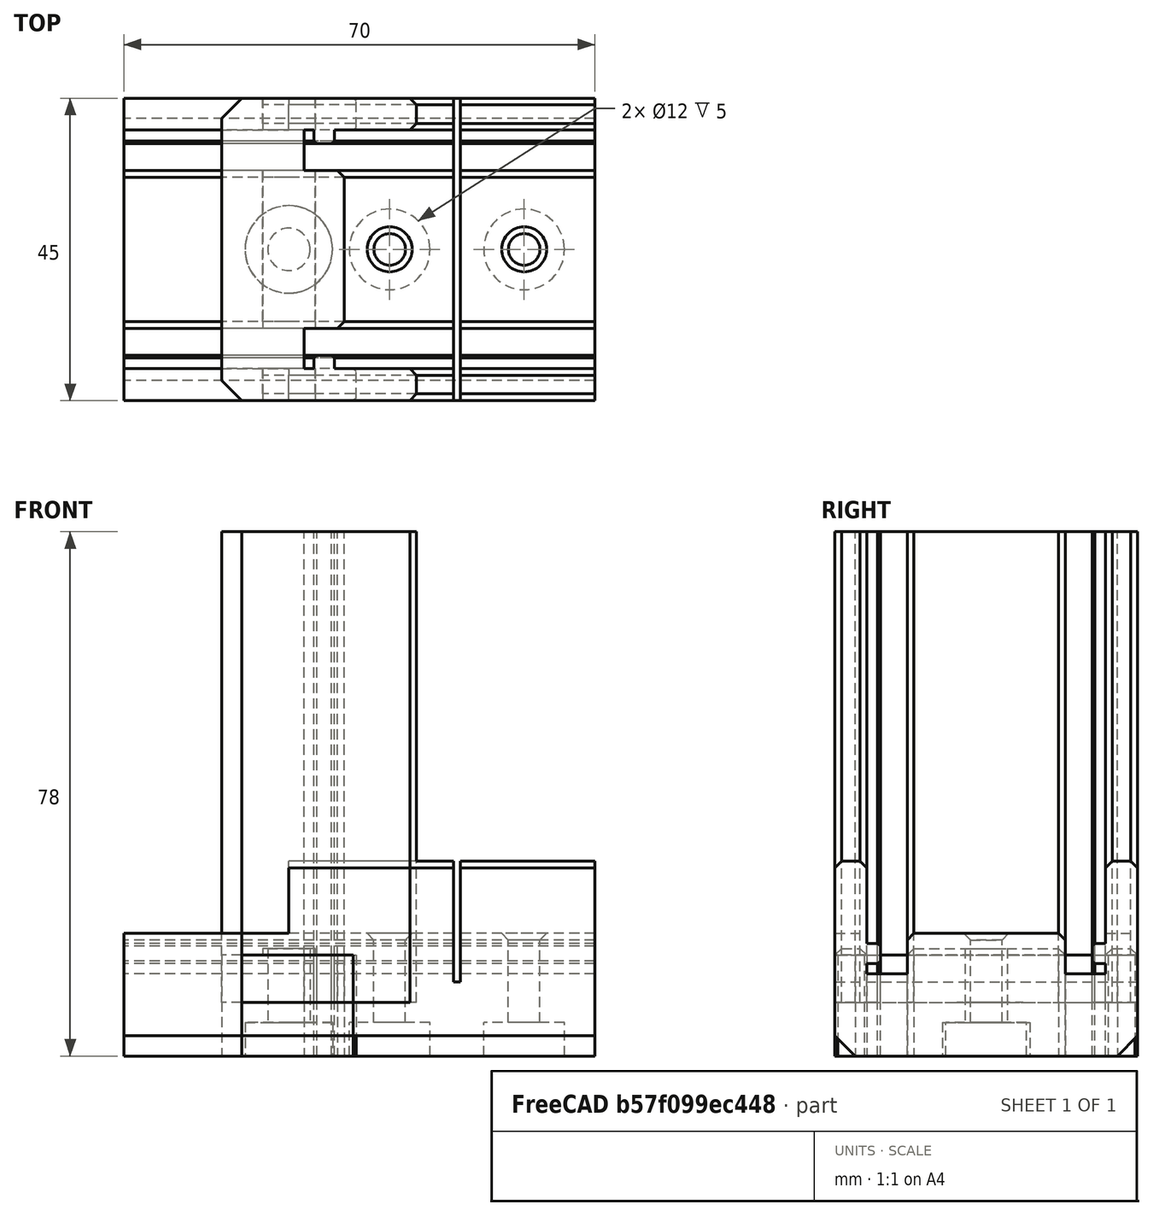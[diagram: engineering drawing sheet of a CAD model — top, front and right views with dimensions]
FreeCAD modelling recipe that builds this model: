
FCSTD DOCUMENT  (FreeCAD 0.19R24291 (Git))
Label: back-panel-dien-alt
License: Other
LicenseURL: GPL3
objects: Part::Box×6, Part::MultiFuse×5, Part::Chamfer×4, Part::Cylinder×4, Part::Cut×4, Part::Feature×2, Part::Refine×2, Part::Extrusion×1, PartDesign::FeatureBase×1, Sketcher::SketchObject×1, PartDesign::Pad×1, PartDesign::Body×1
note: 33 computed .brp shape members not serialized (recipe doc carries the construction recipe); baked Part::Feature solids carry a one-line shape summary decoded from their .brp

FEATURE [Part::Feature] Cut008004003004014002002005003004001  label="din-stopper003"
  Placement = pos=(-5,-22.5,15) rot=(0.57735,-0.57735,-0.57735;4.18879rad)
  shape: bbox 20 x 45 x 16 mm, 43 faces (baked)
FEATURE [Part::Box] Box  label="Cube"
  AttacherType = Attacher::AttachEngine3D
  Height = 15
  Length = 3
  Placement = pos=(-21.25,-17.75,0) rot=(0,0,1;0rad)
  Width = 2
FEATURE [Part::Box] Box001  label="Cube001"
  AttacherType = Attacher::AttachEngine3D
  Height = 15
  Length = 3
  Placement = pos=(-21.25,15.75,0) rot=(0,0,1;0rad)
  Width = 2
FEATURE [Part::Chamfer] Chamfer
  Base = -> Box001
  Edges = 2 edges r=0.4: [Edge1,Edge5]
FEATURE [Part::Chamfer] Chamfer001
  Base = -> Box
  Edges = 2 edges r=0.4: [Edge3,Edge7]
FEATURE [Part::MultiFuse] Fusion
  Shapes = -> [Chamfer,Chamfer001,Cut008004003004014002002005003004001]
FEATURE [Part::Refine] Fusion001
  Source = -> Fusion
FEATURE [Part::Feature] Fusion001_cs
  shape: bbox 20 x 45 x 4e-07 mm, 0 faces, 0 solids (baked)
FEATURE [Part::Extrusion] Extrude
  Base = -> Fusion001_cs
  Dir = (0,0,1)
  DirMode = 2
  FaceMakerClass = Part::FaceMakerBullseye
  LengthFwd = 70
  LengthRev = 0
  Solid = true
  Symmetric = false
FEATURE [Part::Box] Box002  label="Cube002"
  AttacherType = Attacher::AttachEngine3D
  Height = 70
  Length = 10
  Placement = pos=(-16,17.75,8) rot=(0,0,1;0rad)
  Width = 4.75
FEATURE [Part::Box] Box003  label="Cube003"
  AttacherType = Attacher::AttachEngine3D
  Height = 70
  Length = 10
  Placement = pos=(-16,-22.5,8) rot=(0,0,1;0rad)
  Width = 4.75
FEATURE [Part::MultiFuse] Fusion002
  Shapes = -> [Box003,Box002]
FEATURE [Part::Chamfer] Chamfer002
  Base = -> Fusion002
  Edges = 4 edges r=1: [Edge5,Edge7,Edge17,Edge19]
FEATURE [Part::MultiFuse] Fusion003
  Shapes = -> [Chamfer002,Extrude]
FEATURE [Part::Box] Box004  label="Cube004"
  AttacherType = Attacher::AttachEngine3D
  Height = 1
  Length = 20
  Placement = pos=(-24,-25,28) rot=(0,0,1;0rad)
  Width = 50
FEATURE [Part::Cylinder] Cylinder
  Angle = 360
  AttacherType = Attacher::AttachEngine3D
  Height = 5
  Placement = pos=(-10,0,0) rot=(0,0,1;0rad)
  Radius = 6
FEATURE [Part::Cylinder] Cylinder001
  Angle = 360
  AttacherType = Attacher::AttachEngine3D
  Height = 5
  Placement = pos=(10,0,0) rot=(0,0,1;0rad)
  Radius = 6
FEATURE [Part::Cylinder] Cylinder002
  Angle = 360
  AttacherType = Attacher::AttachEngine3D
  Height = 32
  Placement = pos=(10,0,0) rot=(0,0,1;0rad)
  Radius = 2.35
FEATURE [Part::Cylinder] Cylinder003
  Angle = 360
  AttacherType = Attacher::AttachEngine3D
  Height = 32
  Placement = pos=(-10,0,0) rot=(0,0,1;0rad)
  Radius = 2.35
FEATURE [Part::MultiFuse] Fusion004
  Shapes = -> [Cylinder003,Cylinder002]
FEATURE [PartDesign::FeatureBase] BaseFeature
  BaseFeature = -> Fusion003
FEATURE [Sketcher::SketchObject] Sketch
  FullyConstrained = false
  MapMode = 5
  Placement = pos=(-8e-16,0,78) rot=(0,0,1;0rad)
  Support = -> [BaseFeature]
  sketch-geometry (1):
    g0: Circle CenterX=-24.8183 CenterY=0.577738 CenterZ=0 NormalX=0 NormalY=0 NormalZ=1 AngleXU=0 Radius=5.04841
FEATURE [PartDesign::Pad] Pad
  BaseFeature = -> BaseFeature
  Direction = (1,1,1)
  Length = 70
  Length2 = 100
  Profile = -> Sketch
  Reversed = true
  Type = 0
FEATURE [PartDesign::Body] Body
  BaseFeature = -> Fusion003
  Group = -> [BaseFeature,Sketch,Pad]
  Origin = -> Origin
  Tip = -> Pad
FEATURE [Part::Cut] Cut
  Base = -> Pad
  Placement = pos=(28.5,0,35) rot=(0,-1,0;1.5708rad)
  Tool = -> Box004
FEATURE [Part::Cut] Cut008004003004014002002005003004002
  Base = -> Cut
  Tool = -> Fusion004
FEATURE [Part::Chamfer] Chamfer003
  Base = -> Cut008004003004014002002005003004002
  Edges = 2 edges r=1: [Edge44,Edge191]
FEATURE [Part::MultiFuse] Fusion005
  Shapes = -> [Cylinder001,Cylinder]
FEATURE [Part::Cut] Cut008004003004014002002005003004003
  Base = -> Chamfer003
  Tool = -> Fusion005
FEATURE [Part::Box] Box005  label="Cube005"
  AttacherType = Attacher::AttachEngine3D
  Height = 16
  Length = 26
  Placement = pos=(-51,-25,18.25) rot=(0,0,1;0rad)
  Width = 49
FEATURE [Part::Cut] Cut008004003004014002002005003004004
  Base = -> Cut008004003004014002002005003004003
  Tool = -> Box005
FEATURE [Part::Refine] Fusion001001
  Source = -> Fusion001
